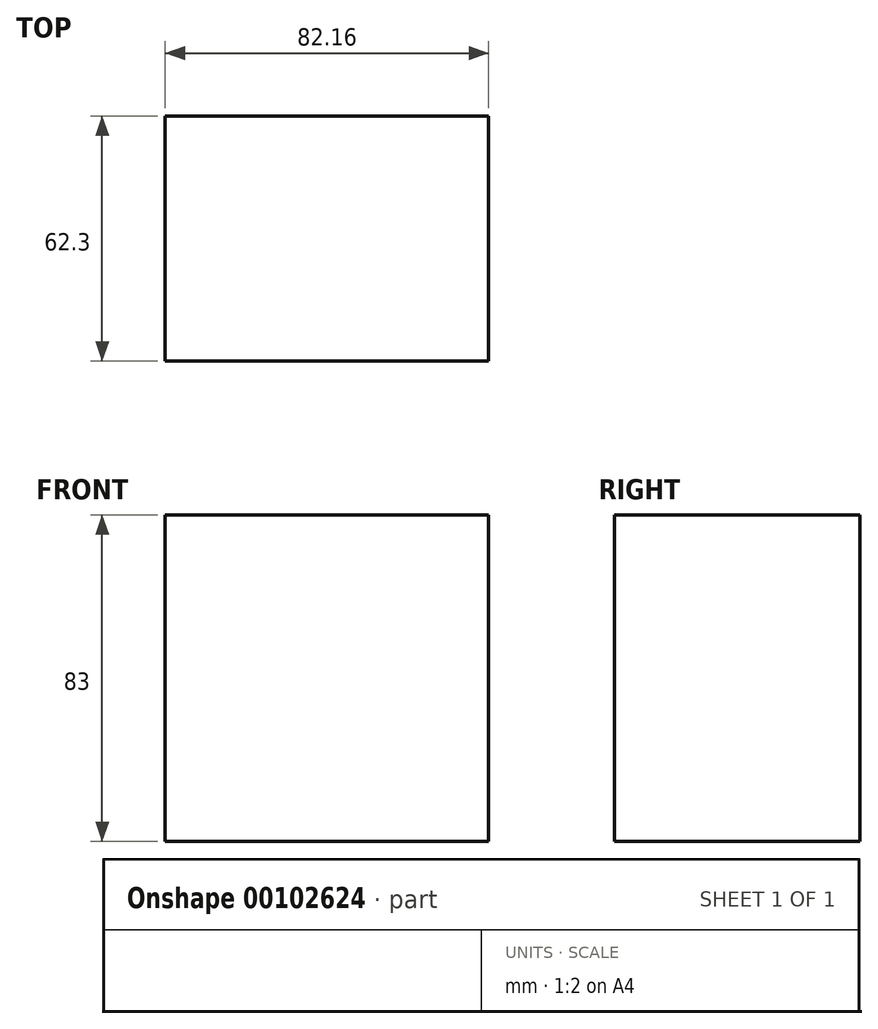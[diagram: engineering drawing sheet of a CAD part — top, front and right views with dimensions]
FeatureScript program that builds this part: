
annotation { "Feature Type Name" : "Feature", "Feature Type Description" : "" }
export const myFeature = defineFeature(function(context is Context, id is Id, definition is map)
    precondition{}
    {
        {
            var Q0;
            Q0=qCreatedBy(makeId("Front.planeOp"),FACE);
            var sketch = newSketch(context, id + "F0", { "sketchPlane" : qUnion([Q0])});
            skLineSegment(sketch, "E0.bottom", {"start": v(41.08, 28.8) * mm, "end": v(-41.08, 28.8) * mm});
            skLineSegment(sketch, "E0.top", {"start": v(41.08, -28.8) * mm, "end": v(-41.08, -28.8) * mm});
            skLineSegment(sketch, "E0.left", {"start": v(41.08, 28.8) * mm, "end": v(41.08, -28.8) * mm});
            skLineSegment(sketch, "E0.right", {"start": v(-41.08, 28.8) * mm, "end": v(-41.08, -28.8) * mm});
            skPoint(sketch, "E0.middle", {"position": v(0, 0) * mm});
            skSolve(sketch);
        }
        {
            var Q0;
            Q0=makeQuery(id+"F0.imprint","IMPRINT",FACE,{"disambiguationData":[TD([[makeQuery(id+"F0.imprint","IMPRINT",EDGE,{"derivedFrom":sQuery(id+"F0.wireOp",EDGE,"E0.bottom")}),1.0]])]});
            extrude(context, id + "F1", {"entities" : qUnion([Q0]), "endBound" : BoundingType.SYMMETRIC, "depth" : 62.3 * mm});
        }
        {
            var Q0;
            Q0=makeQuery(id+"F1.opExtrude","SWEPT_FACE",FACE,{"disambiguationData":[OSD([sQuery(id+"F0.wireOp",EDGE,"E0.bottom")])]});
            extrude(context, id + "F2", {"entities" : qUnion([Q0]), "operationType" : NewBodyOperationType.ADD, "depth" : 25.4 * mm});
        }
    });
